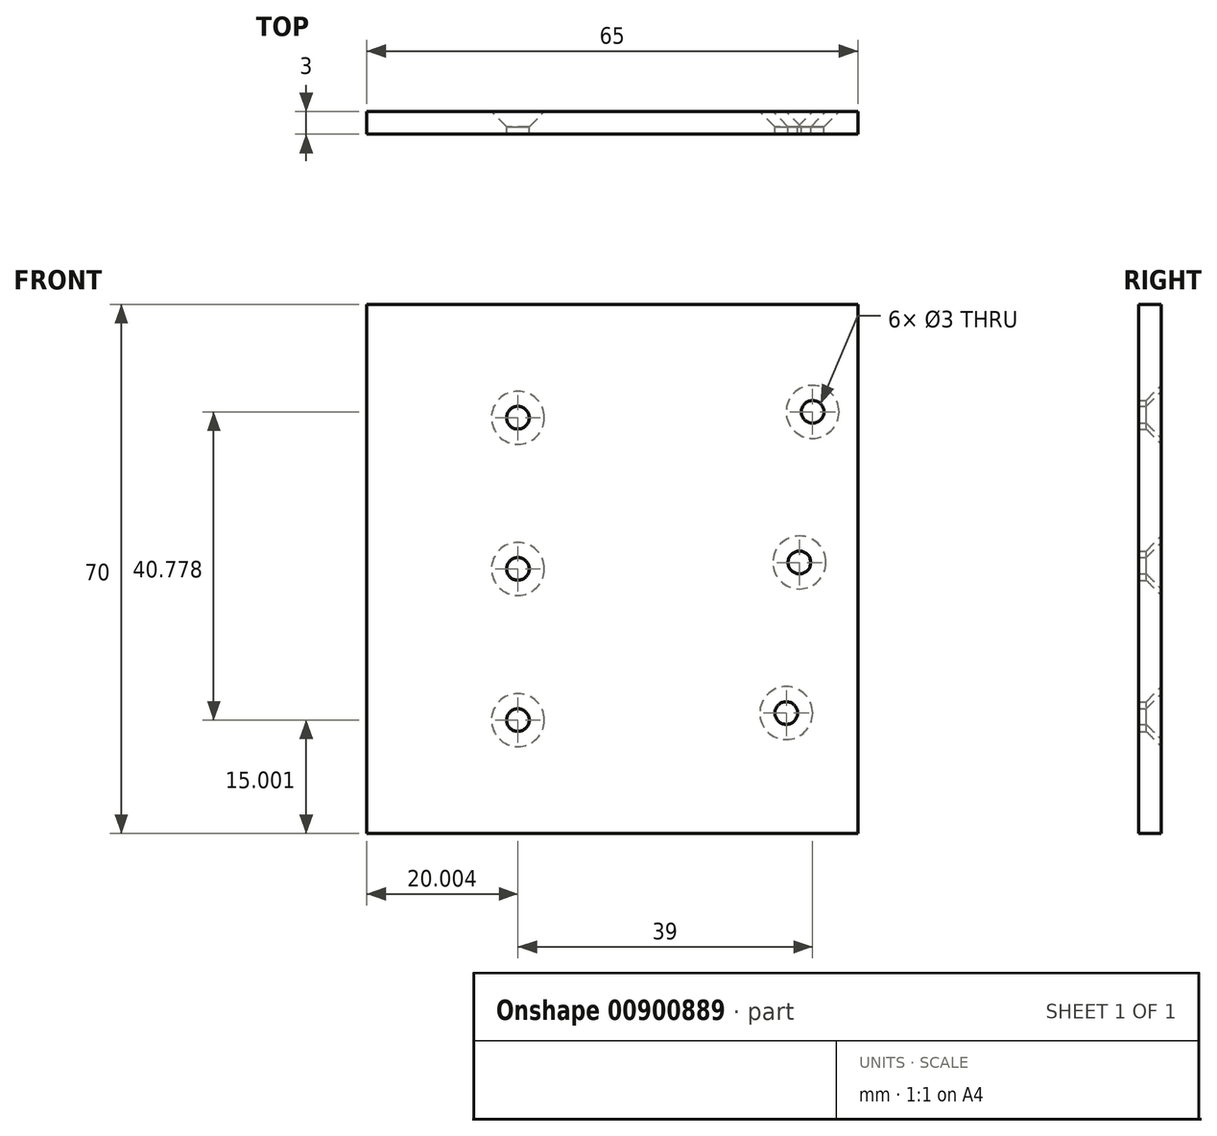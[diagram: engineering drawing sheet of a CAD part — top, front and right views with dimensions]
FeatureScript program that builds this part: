
annotation { "Feature Type Name" : "Feature", "Feature Type Description" : "" }
export const myFeature = defineFeature(function(context is Context, id is Id, definition is map)
    precondition{}
    {
        {
            var Q0;
            Q0=qCreatedBy(makeId("Front.planeOp"),FACE);
            var sketch = newSketch(context, id + "F0", { "sketchPlane" : qUnion([Q0])});
            skLineSegment(sketch, "E0.bottom", {"start": v(-26.6, 28.87) * mm, "end": v(38.4, 28.87) * mm});
            skLineSegment(sketch, "E0.top", {"start": v(-26.6, -41.13) * mm, "end": v(38.4, -41.13) * mm});
            skLineSegment(sketch, "E0.left", {"start": v(-26.6, 28.87) * mm, "end": v(-26.6, -41.13) * mm});
            skLineSegment(sketch, "E0.right", {"start": v(38.4, 28.87) * mm, "end": v(38.4, -41.13) * mm});
            skLineSegment(sketch, "E1", {"start": v(-6.6, 28.87) * mm, "end": v(-6.6, 13.87) * mm, "construction": true});
            skLineSegment(sketch, "E2", {"start": v(-6.6, 13.87) * mm, "end": v(-6.6, -6.13) * mm, "construction": true});
            skLineSegment(sketch, "E3", {"start": v(-6.6, -6.13) * mm, "end": v(-6.6, -26.13) * mm, "construction": true});
            skCircle(sketch, "E4", {"center": v(-6.6, 13.87) * mm, "radius": 1.5 * mm});
            skCircle(sketch, "E5", {"center": v(-6.6, -6.13) * mm, "radius": 1.5 * mm});
            skCircle(sketch, "E6", {"center": v(-6.6, -26.13) * mm, "radius": 1.5 * mm});
            skCircle(sketch, "E7", {"center": v(32.4, 14.65) * mm, "radius": 1.5 * mm});
            skCircle(sketch, "E8", {"center": v(28.92, -25.2) * mm, "radius": 1.5 * mm});
            skLineSegment(sketch, "E9", {"start": v(32.4, 14.65) * mm, "end": v(38.4, 14.65) * mm, "construction": true});
            skLineSegment(sketch, "E10", {"start": v(32.4, 14.65) * mm, "end": v(32.4, 28.87) * mm, "construction": true});
            skLineSegment(sketch, "E11", {"start": v(32.4, 14.65) * mm, "end": v(30.66, -5.28) * mm, "construction": true});
            skLineSegment(sketch, "E12", {"start": v(28.92, -25.2) * mm, "end": v(30.66, -5.28) * mm, "construction": true});
            skCircle(sketch, "E13", {"center": v(30.66, -5.28) * mm, "radius": 1.5 * mm});
            skSolve(sketch);
        }
        {
            var Q0;
            Q0 = qSketchRegion(id + "F0", true);
            extrude(context, id + "F1", {"entities" : qUnion([Q0]), "depth" : 3 * mm, "offsetDistance" : 25 * mm});
        }
        {
            var Q0;
            Q0=makeQuery(id+"F1.opExtrude","CAP_EDGE",EDGE,{"disambiguationData":[OSD([sQuery(id+"F0.wireOp",EDGE,"E7")])],"isStart":true});
            var Q1;
            Q1=makeQuery(id+"F1.opExtrude","CAP_EDGE",EDGE,{"disambiguationData":[OSD([sQuery(id+"F0.wireOp",EDGE,"E4")])],"isStart":true});
            var Q2;
            Q2=makeQuery(id+"F1.opExtrude","CAP_EDGE",EDGE,{"disambiguationData":[OSD([sQuery(id+"F0.wireOp",EDGE,"E13")])],"isStart":true});
            var Q3;
            Q3=makeQuery(id+"F1.opExtrude","CAP_EDGE",EDGE,{"disambiguationData":[OSD([sQuery(id+"F0.wireOp",EDGE,"E5")])],"isStart":true});
            var Q4;
            Q4=makeQuery(id+"F1.opExtrude","CAP_EDGE",EDGE,{"disambiguationData":[OSD([sQuery(id+"F0.wireOp",EDGE,"E6")])],"isStart":true});
            var Q5;
            Q5=makeQuery(id+"F1.opExtrude","CAP_EDGE",EDGE,{"disambiguationData":[OSD([sQuery(id+"F0.wireOp",EDGE,"E8")])],"isStart":true});
            chamfer(context, id + "F2", {"entities" : qUnion([Q0, Q1, Q2, Q3, Q4, Q5]), "width" : 2 * mm, "tangentPropagation" : true});
        }
    });
